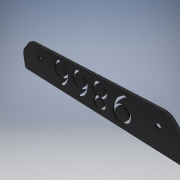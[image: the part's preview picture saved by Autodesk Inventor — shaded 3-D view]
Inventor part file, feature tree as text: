
AUTODESK INVENTOR PART (.ipt)
format: ipt  version: 2018.3 (Build 223284000, 284)  size: 585,216 bytes
history: native  units: mm
features: extrude x9, sketch x9, projected_geometry x8, fillet x1
ambient origin geometry x8: Origin, YZ Plane, XZ Plane, XY Plane, X Axis, Y Axis, Z Axis, Center Point
bodies: Solid1 (feature_tree), Body1 (feature_tree)
feature tree (27):
  extrude  "Extrusion1"  Depth=22.5mm
  extrude  "Extrusion2"  Depth=34.677mm
  extrude  "Extrusion3"  Depth=3.1mm
  fillet  "Fillet1"  Radius=7.5mm
  extrude  "Extrusion4"  Depth=10.0mm TaperAngle=0.0deg
  extrude  "Extrusion5"  Depth=3.1mm
  extrude  "Extrusion6"  Depth=7.5mm
  extrude  "Extrusion7"  Depth=7.5mm
  extrude  "Extrusion10"  Depth=5.0mm TaperAngle=0.0deg
  extrude  "Extrusion11"  Depth=10.0mm TaperAngle=0.0deg
  sketch  "Sketch1"  dims[d0=22.5mm d1=22.5mm]
  sketch  "Sketch2"  dims[d2=10.0mm d3=0.0mm d4=34.677mm]
  sketch  "Sketch3"  dims[d6=10.0mm d7=0.0mm d8=3.1mm d9=7.5mm]
  sketch  "Sketch4"  dims[d10=10.0mm d11=10.0mm d12=0.0mm]
  projected_geometry  "Projected Loop1"
  sketch  "Sketch5"  dims[d13=5.0mm d14=3.1mm]
  projected_geometry  "Projected Loop2"
  sketch  "Sketch6"  dims[d15=7.5mm d16=7.5mm]
  sketch  "Sketch7"  dims[d17=3.1mm d18=7.5mm]
  sketch  "Sketch11"  dims[d19=7.5mm d20=5.0mm d21=0.0mm]
  sketch  "Sketch12"  dims[d22=5.0mm d23=0.0mm d24=10.0mm d25=0.0mm d26=10.0mm d27=0.0mm d36=0.0mm d37=0.0mm d38=2.0mm d39=2.0mm d40=2.0mm d41=2.0mm d42=5.0mm d43=0.0mm]
  projected_geometry  "Projected Loop4"
  projected_geometry  "Projected Loop5"
  projected_geometry  "Projected Loop6"
  projected_geometry  "Projected Loop7"
  projected_geometry  "Projected Loop8"
  projected_geometry  "Projected Loop9"
